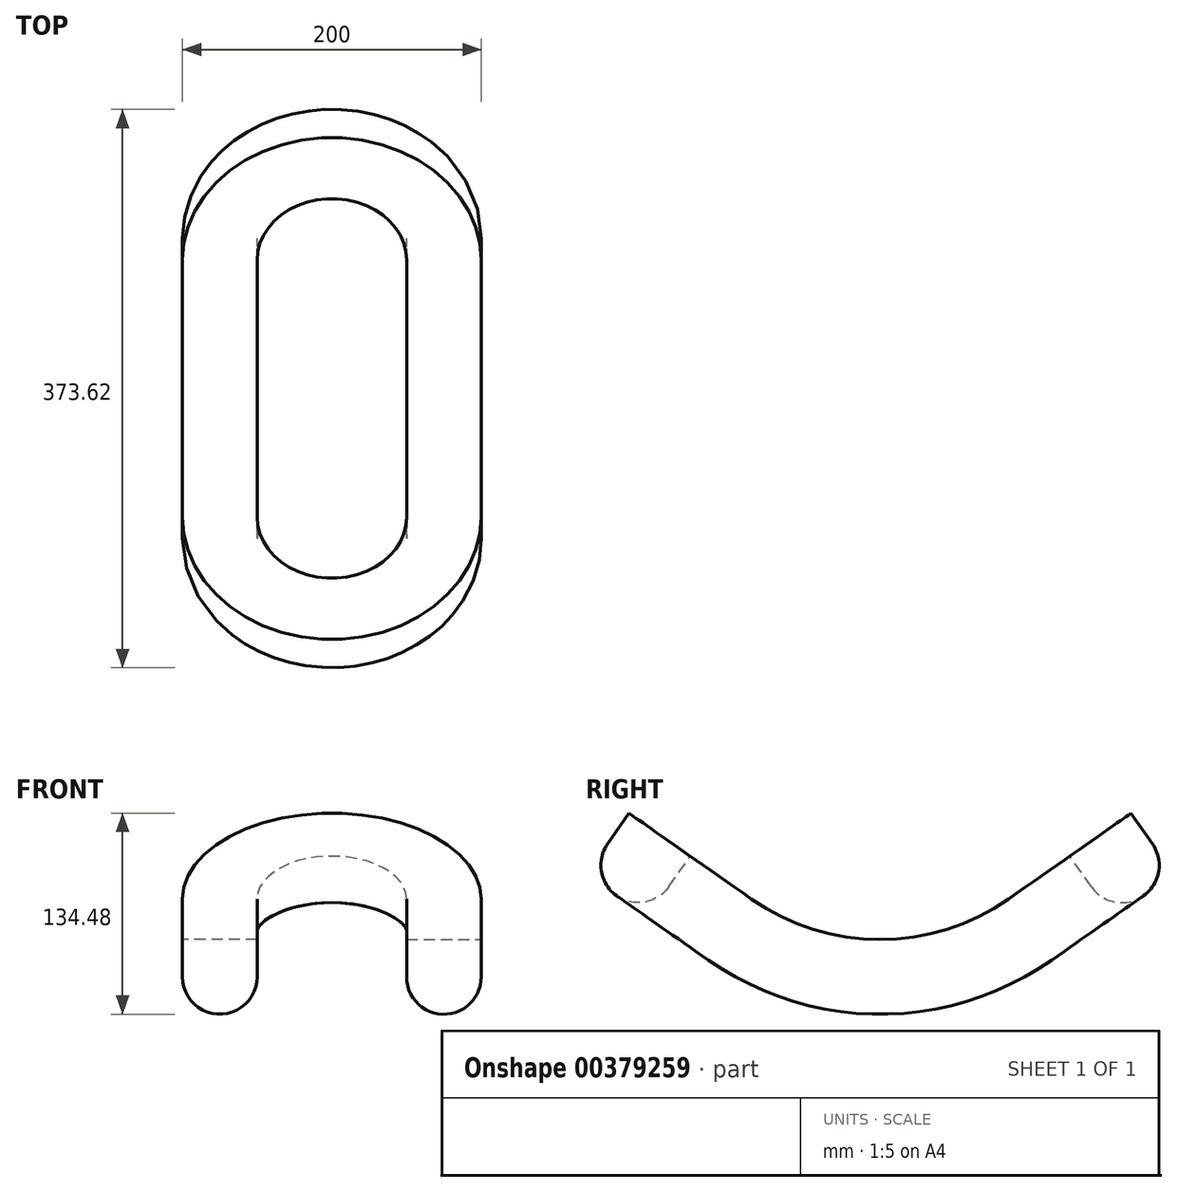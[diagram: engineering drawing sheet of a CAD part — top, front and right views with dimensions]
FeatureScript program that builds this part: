
annotation { "Feature Type Name" : "Feature", "Feature Type Description" : "" }
export const myFeature = defineFeature(function(context is Context, id is Id, definition is map)
    precondition{}
    {
        {
            var Q0;
            Q0=qCreatedBy(makeId("Right.planeOp"),FACE);
            var sketch = newSketch(context, id + "F0", { "sketchPlane" : qUnion([Q0])});
            skArc(sketch, "E0", {"start": v(0, 0) * mm, "mid": v(45.1, 6.94) * mm, "end": v(86.04, 27.13) * mm});
            skLineSegment(sketch, "E1", {"start": v(0, 150) * mm, "end": v(86.04, 27.13) * mm, "construction": true});
            skLineSegment(sketch, "E2", {"start": v(0, 0) * mm, "end": v(0, 150) * mm, "construction": true});
            skLineSegment(sketch, "E3", {"start": v(86.04, 27.13) * mm, "end": v(167.95, 84.48) * mm});
            skSolve(sketch);
        }
        {
            var Q0;
            Q0=sQuery(id+"F0.wireOp",EDGE,"E3");
            var Q1;
            Q1=sQuery(id+"F0.wireOp",EDGE,"E0");
            extrude(context, id + "F1", {"bodyType" : ToolBodyType.SURFACE, "surfaceEntities" : qUnion([Q0, Q1]), "depth" : 100 * mm});
        }
        {
            var Q0;
            Q0=makeQuery(id+"F1.opExtrude","SWEPT_FACE",FACE,{"disambiguationData":[OSD([sQuery(id+"F0.wireOp",EDGE,"E3")])]});
            var sketch = newSketch(context, id + "F2", { "sketchPlane" : qUnion([Q0])});
            skArc(sketch, "E4", {"start": v(0, -186.04) * mm, "mid": v(70.71, -156.75) * mm, "end": v(100, -86.04) * mm});
            skSolve(sketch);
        }
        {
            var Q0;
            Q0=qCreatedBy(makeId("Front.planeOp"),FACE);
            var sketch = newSketch(context, id + "F3", { "sketchPlane" : qUnion([Q0])});
            skLineSegment(sketch, "E5.bottom", {"start": v(100, 0) * mm, "end": v(50, 0) * mm});
            skLineSegment(sketch, "E5.top", {"start": v(100, -25) * mm, "end": v(50, -25) * mm, "construction": true});
            skLineSegment(sketch, "E5.left", {"start": v(100, 0) * mm, "end": v(100, -25) * mm});
            skLineSegment(sketch, "E5.right", {"start": v(50, 0) * mm, "end": v(50, -25) * mm});
            skArc(sketch, "E6", {"start": v(50, -25) * mm, "mid": v(75, -50) * mm, "end": v(100, -25) * mm});
            skSolve(sketch);
        }
        {
            var Q0;
            Q0=makeQuery(id+"F3.imprint","IMPRINT",FACE,{"disambiguationData":[TD([[makeQuery(id+"F3.imprint","IMPRINT",EDGE,{"derivedFrom":sQuery(id+"F3.wireOp",EDGE,"E5.bottom")}),1.0]])]});
            var Q1;
            Q1=makeQuery(id+"F1.opExtrude","CAP_EDGE",EDGE,{"disambiguationData":[OSD([sQuery(id+"F0.wireOp",EDGE,"E0")])],"isStart":false});
            var Q2;
            Q2=sQuery(id+"F2.wireOp",EDGE,"E4");
            sweep(context, id + "F4", {"profiles" : qUnion([Q0]), "path" : qUnion([Q1, Q2])});
        }
        {
            var Q0;
            Q0=makeQuery(id+"F4.opSweep","SWEPT_BODY",BODY,{"disambiguationData":[OSD([sQuery(id+"F2.wireOp",EDGE,"E4"),sQuery(id+"F3.wireOp",EDGE,"E5.bottom"),sQuery(id+"F3.wireOp",EDGE,"E5.left"),sQuery(id+"F3.wireOp",EDGE,"E5.right"),sQuery(id+"F3.wireOp",EDGE,"E6")])]});
            var Q1;
            Q1=qCreatedBy(makeId("Right.planeOp"),FACE);
            mirror(context, id + "F5", {"operationType" : NewBodyOperationType.ADD, "entities" : qUnion([Q0]), "mirrorPlane" : qUnion([Q1])});
        }
        {
            var Q0;
            Q0=makeQuery(id+"F4.opSweep","SWEPT_BODY",BODY,{"disambiguationData":[OSD([sQuery(id+"F2.wireOp",EDGE,"E4"),sQuery(id+"F3.wireOp",EDGE,"E5.bottom"),sQuery(id+"F3.wireOp",EDGE,"E5.left"),sQuery(id+"F3.wireOp",EDGE,"E5.right"),sQuery(id+"F3.wireOp",EDGE,"E6")])]});
            var Q1;
            Q1=qCreatedBy(makeId("Front.planeOp"),FACE);
            mirror(context, id + "F6", {"operationType" : NewBodyOperationType.ADD, "entities" : qUnion([Q0]), "mirrorPlane" : qUnion([Q1])});
        }
    });
